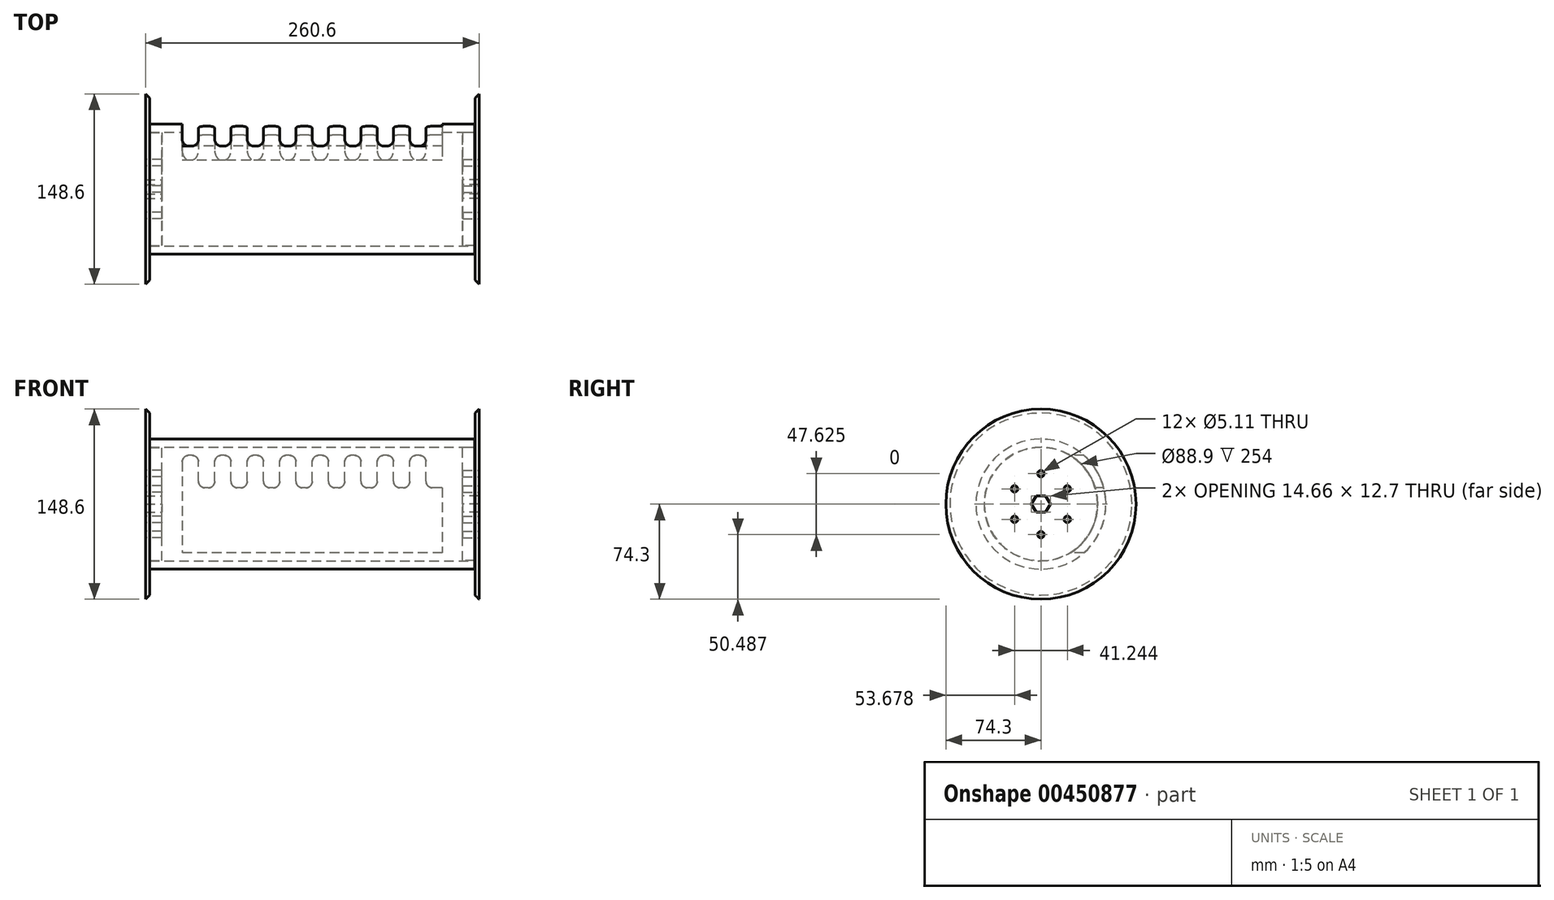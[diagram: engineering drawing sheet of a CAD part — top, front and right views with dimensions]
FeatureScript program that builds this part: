
annotation { "Feature Type Name" : "Feature", "Feature Type Description" : "" }
export const myFeature = defineFeature(function(context is Context, id is Id, definition is map)
    precondition{}
    {
        {
            var Q0;
            Q0=qCreatedBy(makeId("Right.planeOp"),FACE);
            var sketch = newSketch(context, id + "F0", { "sketchPlane" : qUnion([Q0])});
            skCircle(sketch, "E0", {"center": v(0, 0) * mm, "radius": 50.8 * mm});
            skSolve(sketch);
        }
        {
            var Q0;
            Q0=makeQuery(id+"F0.imprint","IMPRINT",FACE,{"disambiguationData":[TD([[makeQuery(id+"F0.imprint","IMPRINT",EDGE,{"derivedFrom":sQuery(id+"F0.wireOp",EDGE,"E0")}),1.0]])]});
            extrude(context, id + "F1", {"entities" : qUnion([Q0]), "depth" : 254 * mm});
        }
        {
            var Q0;
            Q0=qCreatedBy(makeId("Front.planeOp"),FACE);
            var sketch = newSketch(context, id + "F2", { "sketchPlane" : qUnion([Q0])});
            skLineSegment(sketch, "E1", {"start": v(0, 0) * mm, "end": v(254, 0) * mm, "construction": true});
            skLineSegment(sketch, "E2.bottom", {"start": v(25.4, 38.1) * mm, "end": v(38.1, 38.1) * mm});
            skLineSegment(sketch, "E2.top", {"start": v(25.4, -38.1) * mm, "end": v(228.6, -38.1) * mm});
            skLineSegment(sketch, "E2.left", {"start": v(25.4, 38.1) * mm, "end": v(25.4, -38.1) * mm});
            skLineSegment(sketch, "E2.right", {"start": v(228.6, 38.1) * mm, "end": v(228.6, -38.1) * mm});
            skPoint(sketch, "E2.middle", {"position": v(127, 0) * mm});
            skLineSegment(sketch, "E3", {"start": v(228.6, 12.7) * mm, "end": v(215.9, 12.7) * mm});
            skLineSegment(sketch, "E4", {"start": v(215.9, 12.7) * mm, "end": v(215.9, 38.1) * mm});
            skLineSegment(sketch, "E5.1.0.1", {"start": v(203.2, 12.7) * mm, "end": v(203.2, 38.1) * mm});
            skLineSegment(sketch, "E5.2.0.0", {"start": v(203.2, 12.7) * mm, "end": v(190.5, 12.7) * mm});
            skLineSegment(sketch, "E5.2.0.1", {"start": v(190.5, 12.7) * mm, "end": v(190.5, 38.1) * mm});
            skLineSegment(sketch, "E5.3.0.1", {"start": v(177.8, 12.7) * mm, "end": v(177.8, 38.1) * mm});
            skLineSegment(sketch, "E5.4.0.0", {"start": v(177.8, 12.7) * mm, "end": v(165.1, 12.7) * mm});
            skLineSegment(sketch, "E5.4.0.1", {"start": v(165.1, 12.7) * mm, "end": v(165.1, 38.1) * mm});
            skLineSegment(sketch, "E5.5.0.1", {"start": v(152.4, 12.7) * mm, "end": v(152.4, 38.1) * mm});
            skLineSegment(sketch, "E5.6.0.0", {"start": v(152.4, 12.7) * mm, "end": v(139.7, 12.7) * mm});
            skLineSegment(sketch, "E5.6.0.1", {"start": v(139.7, 12.7) * mm, "end": v(139.7, 38.1) * mm});
            skLineSegment(sketch, "E5.7.0.1", {"start": v(127, 12.7) * mm, "end": v(127, 38.1) * mm});
            skLineSegment(sketch, "E5.8.0.0", {"start": v(127, 12.7) * mm, "end": v(114.3, 12.7) * mm});
            skLineSegment(sketch, "E5.8.0.1", {"start": v(114.3, 12.7) * mm, "end": v(114.3, 38.1) * mm});
            skLineSegment(sketch, "E5.9.0.1", {"start": v(101.6, 12.7) * mm, "end": v(101.6, 38.1) * mm});
            skLineSegment(sketch, "E5.10.0.0", {"start": v(101.6, 12.7) * mm, "end": v(88.9, 12.7) * mm});
            skLineSegment(sketch, "E5.10.0.1", {"start": v(88.9, 12.7) * mm, "end": v(88.9, 38.1) * mm});
            skLineSegment(sketch, "E5.11.0.1", {"start": v(76.2, 12.7) * mm, "end": v(76.2, 38.1) * mm});
            skLineSegment(sketch, "E5.12.0.0", {"start": v(76.2, 12.7) * mm, "end": v(63.5, 12.7) * mm});
            skLineSegment(sketch, "E5.12.0.1", {"start": v(63.5, 12.7) * mm, "end": v(63.5, 38.1) * mm});
            skLineSegment(sketch, "E5.13.0.1", {"start": v(50.8, 12.7) * mm, "end": v(50.8, 38.1) * mm});
            skLineSegment(sketch, "E5.14.0.0", {"start": v(50.8, 12.7) * mm, "end": v(38.1, 12.7) * mm});
            skLineSegment(sketch, "E5.14.0.1", {"start": v(38.1, 12.7) * mm, "end": v(38.1, 38.1) * mm});
            skLineSegment(sketch, "E5.15.0.1", {"start": v(25.4, 4.2) * mm, "end": v(25.4, 25.4) * mm});
            skLineSegment(sketch, "E6.trimOffspring", {"start": v(203.2, 38.1) * mm, "end": v(215.9, 38.1) * mm});
            skLineSegment(sketch, "E7.trimOffspring", {"start": v(177.8, 38.1) * mm, "end": v(190.5, 38.1) * mm});
            skLineSegment(sketch, "E8.trimOffspring", {"start": v(152.4, 38.1) * mm, "end": v(165.1, 38.1) * mm});
            skLineSegment(sketch, "E9.trimOffspring", {"start": v(127, 38.1) * mm, "end": v(139.7, 38.1) * mm});
            skLineSegment(sketch, "E10.trimOffspring", {"start": v(101.6, 38.1) * mm, "end": v(114.3, 38.1) * mm});
            skLineSegment(sketch, "E11.trimOffspring", {"start": v(76.2, 38.1) * mm, "end": v(88.9, 38.1) * mm});
            skLineSegment(sketch, "E12.trimOffspring", {"start": v(50.8, 38.1) * mm, "end": v(63.5, 38.1) * mm});
            skSolve(sketch);
        }
        {
            var Q0;
            Q0=qSketchRegion(id+"F2",true);
            extrude(context, id + "F3", {"entities" : qUnion([Q0]), "operationType" : NewBodyOperationType.REMOVE, "endBound" : BoundingType.THROUGH_ALL, "oppositeDirection" : true, "depth" : 25.4 * mm});
        }
        {
            var Q0;
            Q0=makeQuery(id+"F1.opExtrude","CAP_FACE",FACE,{"disambiguationData":[OSD([sQuery(id+"F0.wireOp",EDGE,"E0")])],"isStart":false});
            var sketch = newSketch(context, id + "F4", { "sketchPlane" : qUnion([Q0])});
            skCircle(sketch, "E13", {"center": v(0, 0) * mm, "radius": 44.45 * mm});
            skSolve(sketch);
        }
        {
            var Q0;
            Q0=qSketchRegion(id+"F4",true);
            var Q1;
            Q1=makeQuery(id+"F1.opExtrude","CAP_FACE",FACE,{"disambiguationData":[OSD([sQuery(id+"F0.wireOp",EDGE,"E0")])],"isStart":true});
            extrude(context, id + "F5", {"entities" : qUnion([Q0, Q1]), "operationType" : NewBodyOperationType.REMOVE, "endBound" : BoundingType.THROUGH_ALL, "oppositeDirection" : true, "depth" : 25.4 * mm});
        }
        {
            var Q0;
            Q0=makeQuery(id+"F3.boolean.opBoolean","COPY",EDGE,{"derivedFrom":makeQuery(id+"F3.opExtrude","SWEPT_EDGE",EDGE,{"disambiguationData":[OSD([sQuery(id+"F2.wireOp",EDGE,"E5.14.0.0"),sQuery(id+"F2.wireOp",EDGE,"E5.14.0.1")])]})});
            var Q1;
            Q1=makeQuery(id+"F3.boolean.opBoolean","COPY",EDGE,{"derivedFrom":makeQuery(id+"F3.opExtrude","SWEPT_EDGE",EDGE,{"disambiguationData":[OSD([sQuery(id+"F2.wireOp",EDGE,"E5.13.0.1"),sQuery(id+"F2.wireOp",EDGE,"E5.14.0.0")])]})});
            var Q2;
            Q2=makeQuery(id+"F3.boolean.opBoolean","COPY",EDGE,{"derivedFrom":makeQuery(id+"F3.opExtrude","SWEPT_EDGE",EDGE,{"disambiguationData":[OSD([sQuery(id+"F2.wireOp",EDGE,"E5.11.0.1"),sQuery(id+"F2.wireOp",EDGE,"E5.12.0.0")])]})});
            var Q3;
            Q3=makeQuery(id+"F3.boolean.opBoolean","COPY",EDGE,{"derivedFrom":makeQuery(id+"F3.opExtrude","SWEPT_EDGE",EDGE,{"disambiguationData":[OSD([sQuery(id+"F2.wireOp",EDGE,"E5.9.0.1"),sQuery(id+"F2.wireOp",EDGE,"E5.10.0.0")])]})});
            var Q4;
            Q4=makeQuery(id+"F3.boolean.opBoolean","COPY",EDGE,{"derivedFrom":makeQuery(id+"F3.opExtrude","SWEPT_EDGE",EDGE,{"disambiguationData":[OSD([sQuery(id+"F2.wireOp",EDGE,"E5.7.0.1"),sQuery(id+"F2.wireOp",EDGE,"E5.8.0.0")])]})});
            var Q5;
            Q5=makeQuery(id+"F3.boolean.opBoolean","COPY",EDGE,{"derivedFrom":makeQuery(id+"F3.opExtrude","SWEPT_EDGE",EDGE,{"disambiguationData":[OSD([sQuery(id+"F2.wireOp",EDGE,"E5.5.0.1"),sQuery(id+"F2.wireOp",EDGE,"E5.6.0.0")])]})});
            var Q6;
            Q6=makeQuery(id+"F3.boolean.opBoolean","COPY",EDGE,{"derivedFrom":makeQuery(id+"F3.opExtrude","SWEPT_EDGE",EDGE,{"disambiguationData":[OSD([sQuery(id+"F2.wireOp",EDGE,"E5.3.0.1"),sQuery(id+"F2.wireOp",EDGE,"E5.4.0.0")])]})});
            var Q7;
            Q7=makeQuery(id+"F3.boolean.opBoolean","COPY",EDGE,{"derivedFrom":makeQuery(id+"F3.opExtrude","SWEPT_EDGE",EDGE,{"disambiguationData":[OSD([sQuery(id+"F2.wireOp",EDGE,"E5.1.0.1"),sQuery(id+"F2.wireOp",EDGE,"E5.2.0.0")])]})});
            var Q8;
            Q8=makeQuery(id+"F3.boolean.opBoolean","COPY",EDGE,{"derivedFrom":makeQuery(id+"F3.opExtrude","SWEPT_EDGE",EDGE,{"disambiguationData":[OSD([sQuery(id+"F2.wireOp",EDGE,"E5.12.0.0"),sQuery(id+"F2.wireOp",EDGE,"E5.12.0.1")])]})});
            var Q9;
            Q9=makeQuery(id+"F3.boolean.opBoolean","COPY",EDGE,{"derivedFrom":makeQuery(id+"F3.opExtrude","SWEPT_EDGE",EDGE,{"disambiguationData":[OSD([sQuery(id+"F2.wireOp",EDGE,"E5.10.0.0"),sQuery(id+"F2.wireOp",EDGE,"E5.10.0.1")])]})});
            var Q10;
            Q10=makeQuery(id+"F3.boolean.opBoolean","COPY",EDGE,{"derivedFrom":makeQuery(id+"F3.opExtrude","SWEPT_EDGE",EDGE,{"disambiguationData":[OSD([sQuery(id+"F2.wireOp",EDGE,"E5.8.0.0"),sQuery(id+"F2.wireOp",EDGE,"E5.8.0.1")])]})});
            var Q11;
            Q11=makeQuery(id+"F3.boolean.opBoolean","COPY",EDGE,{"derivedFrom":makeQuery(id+"F3.opExtrude","SWEPT_EDGE",EDGE,{"disambiguationData":[OSD([sQuery(id+"F2.wireOp",EDGE,"E5.6.0.0"),sQuery(id+"F2.wireOp",EDGE,"E5.6.0.1")])]})});
            var Q12;
            Q12=makeQuery(id+"F3.boolean.opBoolean","COPY",EDGE,{"derivedFrom":makeQuery(id+"F3.opExtrude","SWEPT_EDGE",EDGE,{"disambiguationData":[OSD([sQuery(id+"F2.wireOp",EDGE,"E5.4.0.0"),sQuery(id+"F2.wireOp",EDGE,"E5.4.0.1")])]})});
            var Q13;
            Q13=makeQuery(id+"F3.boolean.opBoolean","COPY",EDGE,{"derivedFrom":makeQuery(id+"F3.opExtrude","SWEPT_EDGE",EDGE,{"disambiguationData":[OSD([sQuery(id+"F2.wireOp",EDGE,"E5.2.0.0"),sQuery(id+"F2.wireOp",EDGE,"E5.2.0.1")])]})});
            var Q14;
            Q14=makeQuery(id+"F3.boolean.opBoolean","COPY",EDGE,{"derivedFrom":makeQuery(id+"F3.opExtrude","SWEPT_EDGE",EDGE,{"disambiguationData":[OSD([sQuery(id+"F2.wireOp",EDGE,"E3"),sQuery(id+"F2.wireOp",EDGE,"E4")])]})});
            var Q15;
            Q15=makeQuery(id+"F3.boolean.opBoolean","COPY",EDGE,{"derivedFrom":makeQuery(id+"F3.opExtrude","SWEPT_EDGE",EDGE,{"disambiguationData":[OSD([sQuery(id+"F2.wireOp",EDGE,"E2.bottom"),sQuery(id+"F2.wireOp",EDGE,"E5.14.0.1")])]})});
            var Q16;
            Q16=makeQuery(id+"F3.boolean.opBoolean","COPY",EDGE,{"derivedFrom":makeQuery(id+"F3.opExtrude","SWEPT_EDGE",EDGE,{"disambiguationData":[OSD([sQuery(id+"F2.wireOp",EDGE,"E5.12.0.1"),sQuery(id+"F2.wireOp",EDGE,"E12.trimOffspring")])]})});
            var Q17;
            Q17=makeQuery(id+"F3.boolean.opBoolean","COPY",EDGE,{"derivedFrom":makeQuery(id+"F3.opExtrude","SWEPT_EDGE",EDGE,{"disambiguationData":[OSD([sQuery(id+"F2.wireOp",EDGE,"E5.13.0.1"),sQuery(id+"F2.wireOp",EDGE,"E12.trimOffspring")])]})});
            var Q18;
            Q18=makeQuery(id+"F3.boolean.opBoolean","COPY",EDGE,{"derivedFrom":makeQuery(id+"F3.opExtrude","SWEPT_EDGE",EDGE,{"disambiguationData":[OSD([sQuery(id+"F2.wireOp",EDGE,"E5.11.0.1"),sQuery(id+"F2.wireOp",EDGE,"E11.trimOffspring")])]})});
            var Q19;
            Q19=makeQuery(id+"F3.boolean.opBoolean","COPY",EDGE,{"derivedFrom":makeQuery(id+"F3.opExtrude","SWEPT_EDGE",EDGE,{"disambiguationData":[OSD([sQuery(id+"F2.wireOp",EDGE,"E5.10.0.1"),sQuery(id+"F2.wireOp",EDGE,"E11.trimOffspring")])]})});
            var Q20;
            Q20=makeQuery(id+"F3.boolean.opBoolean","COPY",EDGE,{"derivedFrom":makeQuery(id+"F3.opExtrude","SWEPT_EDGE",EDGE,{"disambiguationData":[OSD([sQuery(id+"F2.wireOp",EDGE,"E5.9.0.1"),sQuery(id+"F2.wireOp",EDGE,"E10.trimOffspring")])]})});
            var Q21;
            Q21=makeQuery(id+"F3.boolean.opBoolean","COPY",EDGE,{"derivedFrom":makeQuery(id+"F3.opExtrude","SWEPT_EDGE",EDGE,{"disambiguationData":[OSD([sQuery(id+"F2.wireOp",EDGE,"E5.8.0.1"),sQuery(id+"F2.wireOp",EDGE,"E10.trimOffspring")])]})});
            var Q22;
            Q22=makeQuery(id+"F3.boolean.opBoolean","COPY",EDGE,{"derivedFrom":makeQuery(id+"F3.opExtrude","SWEPT_EDGE",EDGE,{"disambiguationData":[OSD([sQuery(id+"F2.wireOp",EDGE,"E5.7.0.1"),sQuery(id+"F2.wireOp",EDGE,"E9.trimOffspring")])]})});
            var Q23;
            Q23=makeQuery(id+"F3.boolean.opBoolean","COPY",EDGE,{"derivedFrom":makeQuery(id+"F3.opExtrude","SWEPT_EDGE",EDGE,{"disambiguationData":[OSD([sQuery(id+"F2.wireOp",EDGE,"E5.5.0.1"),sQuery(id+"F2.wireOp",EDGE,"E8.trimOffspring")])]})});
            var Q24;
            Q24=makeQuery(id+"F3.boolean.opBoolean","COPY",EDGE,{"derivedFrom":makeQuery(id+"F3.opExtrude","SWEPT_EDGE",EDGE,{"disambiguationData":[OSD([sQuery(id+"F2.wireOp",EDGE,"E5.4.0.1"),sQuery(id+"F2.wireOp",EDGE,"E8.trimOffspring")])]})});
            var Q25;
            Q25=makeQuery(id+"F3.boolean.opBoolean","COPY",EDGE,{"derivedFrom":makeQuery(id+"F3.opExtrude","SWEPT_EDGE",EDGE,{"disambiguationData":[OSD([sQuery(id+"F2.wireOp",EDGE,"E5.6.0.1"),sQuery(id+"F2.wireOp",EDGE,"E9.trimOffspring")])]})});
            var Q26;
            Q26=makeQuery(id+"F3.boolean.opBoolean","COPY",EDGE,{"derivedFrom":makeQuery(id+"F3.opExtrude","SWEPT_EDGE",EDGE,{"disambiguationData":[OSD([sQuery(id+"F2.wireOp",EDGE,"E5.3.0.1"),sQuery(id+"F2.wireOp",EDGE,"E7.trimOffspring")])]})});
            var Q27;
            Q27=makeQuery(id+"F3.boolean.opBoolean","COPY",EDGE,{"derivedFrom":makeQuery(id+"F3.opExtrude","SWEPT_EDGE",EDGE,{"disambiguationData":[OSD([sQuery(id+"F2.wireOp",EDGE,"E5.1.0.1"),sQuery(id+"F2.wireOp",EDGE,"E6.trimOffspring")])]})});
            var Q28;
            Q28=makeQuery(id+"F3.boolean.opBoolean","COPY",EDGE,{"derivedFrom":makeQuery(id+"F3.opExtrude","SWEPT_EDGE",EDGE,{"disambiguationData":[OSD([sQuery(id+"F2.wireOp",EDGE,"E5.2.0.1"),sQuery(id+"F2.wireOp",EDGE,"E7.trimOffspring")])]})});
            var Q29;
            Q29=makeQuery(id+"F3.boolean.opBoolean","COPY",EDGE,{"derivedFrom":makeQuery(id+"F3.opExtrude","SWEPT_EDGE",EDGE,{"disambiguationData":[OSD([sQuery(id+"F2.wireOp",EDGE,"E4"),sQuery(id+"F2.wireOp",EDGE,"E6.trimOffspring")])]})});
            var Q30;
            Q30=makeQuery(id+"F3.boolean.opBoolean","COPY",EDGE,{"derivedFrom":makeQuery(id+"F3.opExtrude","SWEPT_EDGE",EDGE,{"disambiguationData":[OSD([sQuery(id+"F2.wireOp",EDGE,"E2.bottom"),sQuery(id+"F2.wireOp",EDGE,"E2.left")])]})});
            fillet(context, id + "F6", {"entities" : qUnion([Q0, Q1, Q2, Q3, Q4, Q5, Q6, Q7, Q8, Q9, Q10, Q11, Q12, Q13, Q14, Q15, Q16, Q17, Q18, Q19, Q20, Q21, Q22, Q23, Q24, Q25, Q26, Q27, Q28, Q29, Q30]), "radius" : 5.08 * mm, "tangentPropagation" : true, "allowEdgeOverflow" : false});
        }
        {
            var Q0;
            Q0=makeQuery(id+"F1.opExtrude","CAP_FACE",FACE,{"disambiguationData":[OSD([sQuery(id+"F0.wireOp",EDGE,"E0")])],"isStart":false});
            var sketch = newSketch(context, id + "F7", { "sketchPlane" : qUnion([Q0])});
            skCircle(sketch, "E14", {"center": v(0, 0) * mm, "radius": 44.2 * mm});
            skCircle(sketch, "E15.cCircle", {"center": v(0, 0) * mm, "radius": 6.35 * mm, "construction": true});
            skLineSegment(sketch, "E15.0", {"start": v(3.67, -6.35) * mm, "end": v(-3.67, -6.35) * mm});
            skLineSegment(sketch, "E15.1", {"start": v(-3.67, -6.35) * mm, "end": v(-7.33, 0) * mm});
            skLineSegment(sketch, "E15.2", {"start": v(-7.33, 0) * mm, "end": v(-3.67, 6.35) * mm});
            skLineSegment(sketch, "E15.3", {"start": v(-3.67, 6.35) * mm, "end": v(3.67, 6.35) * mm});
            skLineSegment(sketch, "E15.4", {"start": v(3.67, 6.35) * mm, "end": v(7.33, 0) * mm});
            skLineSegment(sketch, "E15.5", {"start": v(7.33, 0) * mm, "end": v(3.67, -6.35) * mm});
            skPoint(sketch, "E15.0.midPoint", {"position": v(0, -6.35) * mm});
            skSolve(sketch);
        }
        {
            var Q0;
            Q0=makeQuery(id+"F7.imprint","IMPRINT",FACE,{"disambiguationData":[TD([[makeQuery(id+"F7.imprint","IMPRINT",EDGE,{"derivedFrom":sQuery(id+"F7.wireOp",EDGE,"E14")}),1.0]])]});
            extrude(context, id + "F8", {"entities" : qUnion([Q0]), "depth" : 0.13 * mm, "hasSecondDirection" : true, "secondDirectionOppositeDirection" : true, "secondDirectionDepth" : 9.52 * mm});
        }
        {
            var Q0;
            Q0=makeQuery(id+"F8.opExtrude","CAP_FACE",FACE,{"disambiguationData":[OSD([sQuery(id+"F7.wireOp",EDGE,"E14"),sQuery(id+"F7.wireOp",EDGE,"E15.0"),sQuery(id+"F7.wireOp",EDGE,"E15.1"),sQuery(id+"F7.wireOp",EDGE,"E15.2"),sQuery(id+"F7.wireOp",EDGE,"E15.3"),sQuery(id+"F7.wireOp",EDGE,"E15.4"),sQuery(id+"F7.wireOp",EDGE,"E15.5")])],"isStart":false});
            var sketch = newSketch(context, id + "F9", { "sketchPlane" : qUnion([Q0])});
            skCircle(sketch, "E16", {"center": v(0, 0) * mm, "radius": 76.2 * mm});
            skCircle(sketch, "E17.cCircle", {"center": v(0, 0) * mm, "radius": 6.35 * mm, "construction": true});
            skLineSegment(sketch, "E17.0", {"start": v(3.67, -6.35) * mm, "end": v(-3.67, -6.35) * mm});
            skLineSegment(sketch, "E17.1", {"start": v(-3.67, -6.35) * mm, "end": v(-7.33, 0) * mm});
            skLineSegment(sketch, "E17.2", {"start": v(-7.33, 0) * mm, "end": v(-3.67, 6.35) * mm});
            skLineSegment(sketch, "E17.3", {"start": v(-3.67, 6.35) * mm, "end": v(3.67, 6.35) * mm});
            skLineSegment(sketch, "E17.4", {"start": v(3.67, 6.35) * mm, "end": v(7.33, 0) * mm});
            skLineSegment(sketch, "E17.5", {"start": v(7.33, 0) * mm, "end": v(3.67, -6.35) * mm});
            skPoint(sketch, "E17.0.midPoint", {"position": v(0, -6.35) * mm});
            skSolve(sketch);
        }
        {
            var Q0;
            Q0=qSketchRegion(id+"F9",true);
            extrude(context, id + "F10", {"entities" : qUnion([Q0]), "operationType" : NewBodyOperationType.ADD, "depth" : 3.17 * mm});
        }
        {
            var Q0;
            Q0=makeQuery(id+"F10.opExtrude","CAP_FACE",FACE,{"disambiguationData":[OSD([sQuery(id+"F9.wireOp",EDGE,"E16"),sQuery(id+"F9.wireOp",EDGE,"E17.0"),sQuery(id+"F9.wireOp",EDGE,"E17.1"),sQuery(id+"F9.wireOp",EDGE,"E17.2"),sQuery(id+"F9.wireOp",EDGE,"E17.3"),sQuery(id+"F9.wireOp",EDGE,"E17.4"),sQuery(id+"F9.wireOp",EDGE,"E17.5")])],"isStart":false});
            var sketch = newSketch(context, id + "F11", { "sketchPlane" : qUnion([Q0])});
            skPoint(sketch, "E18", {"position": v(0, 23.81) * mm});
            skPoint(sketch, "E19.1.0", {"position": v(-20.62, 11.9) * mm});
            skPoint(sketch, "E19.2.0", {"position": v(-20.62, -11.9) * mm});
            skPoint(sketch, "E19.3.0", {"position": v(0, -23.81) * mm});
            skPoint(sketch, "E19.4.0", {"position": v(20.62, -11.9) * mm});
            skPoint(sketch, "E19.5.0", {"position": v(20.62, 11.9) * mm});
            skPoint(sketch, "E19.center", {"position": v(0, 0) * mm});
            skSolve(sketch);
        }
        {
            var Q0;
            Q0=makeQuery(id+"F10.opExtrude","CAP_EDGE",EDGE,{"disambiguationData":[OSD([sQuery(id+"F9.wireOp",EDGE,"E16")])],"isStart":true});
            chamfer(context, id + "F12", {"entities" : qUnion([Q0]), "width" : 5.08 * mm, "tangentPropagation" : true});
        }
        {
            var Q0;
            Q0=sQuery(id+"F11.wireOp",VERTEX,"E18");
            var Q1;
            Q1=sQuery(id+"F11.wireOp",VERTEX,"E19.5.0");
            var Q2;
            Q2=sQuery(id+"F11.wireOp",VERTEX,"E19.4.0");
            var Q3;
            Q3=sQuery(id+"F11.wireOp",VERTEX,"E19.3.0");
            var Q4;
            Q4=sQuery(id+"F11.wireOp",VERTEX,"E19.2.0");
            var Q5;
            Q5=sQuery(id+"F11.wireOp",VERTEX,"E19.1.0");
            var Q6;
            Q6=makeQuery(id+"F8.opExtrude","SWEPT_BODY",BODY,{"disambiguationData":[OSD([sQuery(id+"F7.wireOp",EDGE,"E14"),sQuery(id+"F7.wireOp",EDGE,"E15.0"),sQuery(id+"F7.wireOp",EDGE,"E15.1"),sQuery(id+"F7.wireOp",EDGE,"E15.2"),sQuery(id+"F7.wireOp",EDGE,"E15.3"),sQuery(id+"F7.wireOp",EDGE,"E15.4"),sQuery(id+"F7.wireOp",EDGE,"E15.5")])]});
            hole(context, id + "F13", {"style" : HoleStyle.SIMPLE, "endStyle" : HoleEndStyle.BLIND, "standardTappedOrClearance" : lookupTablePath({ "standard" : "ANSI", "fit" : "Normal (ASME)", "size" : "#10", "type" : "Clearance" }), "standardBlindInLast" : lookupTablePath({ "fit" : "Free", "standard" : "ANSI", "size" : "#10", "type" : "Clearance" }), "holeDiameter" : 5.1 * mm, "holeDepth" : 12.7 * mm, "isTappedThrough" : true, "tappedDepth" : 12.7 * mm, "tapClearance" : 3, "locations" : qUnion([Q0, Q1, Q2, Q3, Q4, Q5]), "scope" : qUnion([Q6])});
        }
        {
            var Q0;
            Q0=makeQuery(id+"F1.opExtrude","CAP_FACE",FACE,{"disambiguationData":[OSD([sQuery(id+"F0.wireOp",EDGE,"E0")])],"isStart":true});
            cPlane(context, id + "F14", {"entities" : qUnion([Q0]), "cplaneType" : CPlaneType.OFFSET, "offset" : 127 * mm, "oppositeDirection" : true, "width" : 152.4 * mm, "height" : 152.4 * mm});
        }
        {
            var Q0;
            Q0=makeQuery(id+"F8.opExtrude","SWEPT_BODY",BODY,{"disambiguationData":[OSD([sQuery(id+"F7.wireOp",EDGE,"E14"),sQuery(id+"F7.wireOp",EDGE,"E15.0"),sQuery(id+"F7.wireOp",EDGE,"E15.1"),sQuery(id+"F7.wireOp",EDGE,"E15.2"),sQuery(id+"F7.wireOp",EDGE,"E15.3"),sQuery(id+"F7.wireOp",EDGE,"E15.4"),sQuery(id+"F7.wireOp",EDGE,"E15.5")])]});
            var Q1;
            Q1=qCreatedBy(id+"F14.planeOp",FACE);
            mirror(context, id + "F15", {"entities" : qUnion([Q0]), "mirrorPlane" : qUnion([Q1])});
        }
    });
